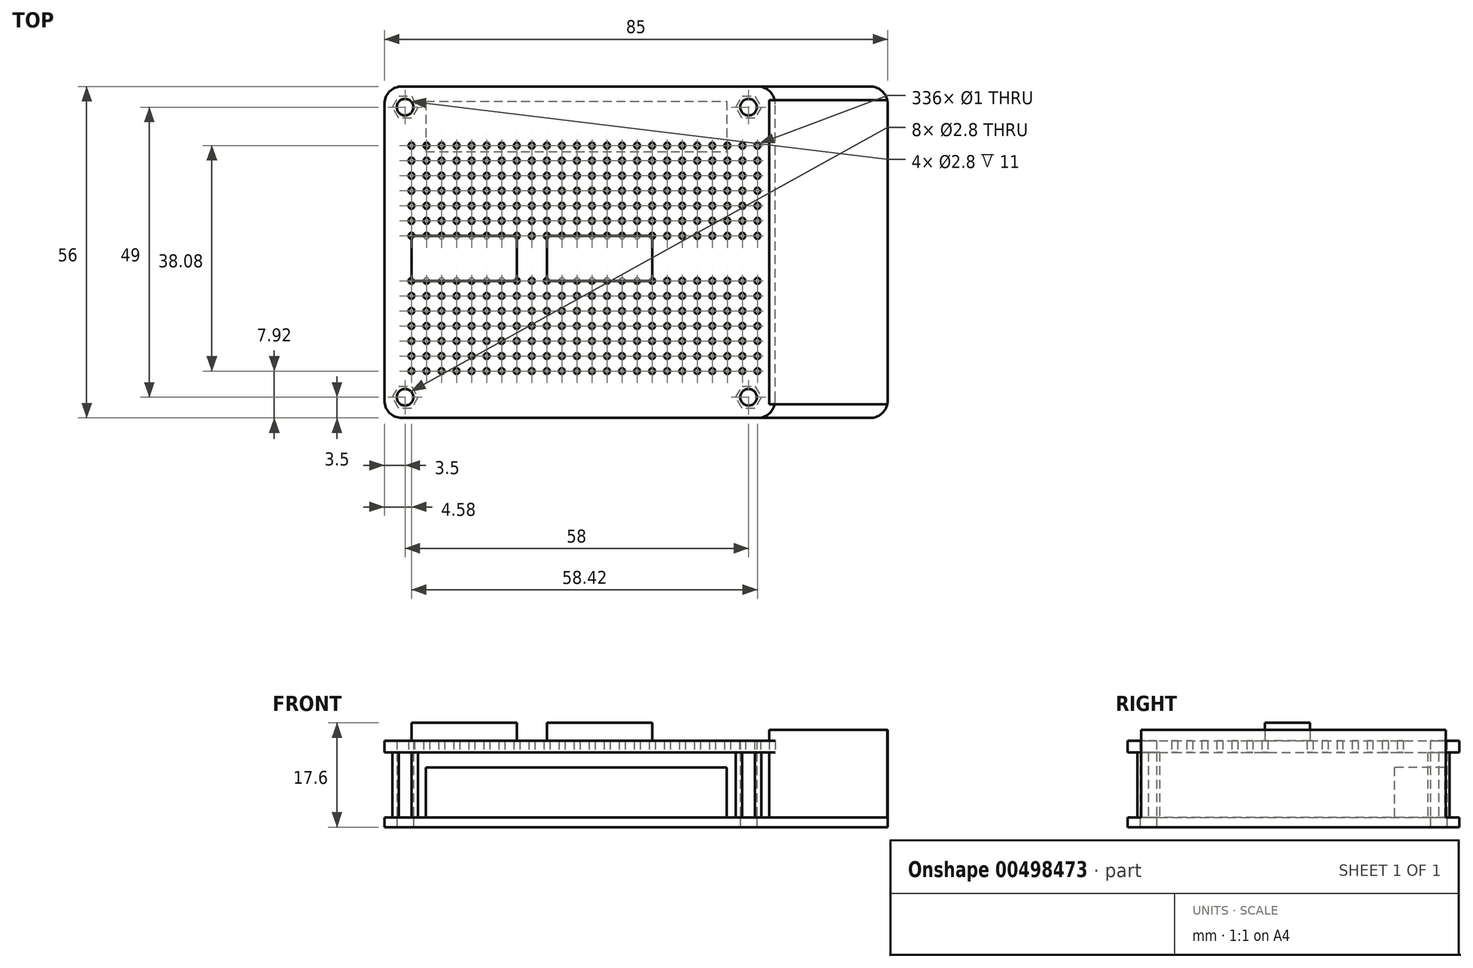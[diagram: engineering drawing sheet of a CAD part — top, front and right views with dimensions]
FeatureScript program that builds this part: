
annotation { "Feature Type Name" : "Feature", "Feature Type Description" : "" }
export const myFeature = defineFeature(function(context is Context, id is Id, definition is map)
    precondition{}
    {
        {
            var Q0;
            Q0=qCreatedBy(makeId("Top.planeOp"),FACE);
            var sketch = newSketch(context, id + "F0", { "sketchPlane" : qUnion([Q0])});
            skLineSegment(sketch, "E0.bottom", {"start": v(39.5, -28) * mm, "end": v(-39.5, -28) * mm});
            skLineSegment(sketch, "E0.top", {"start": v(39.5, 28) * mm, "end": v(-39.5, 28) * mm});
            skLineSegment(sketch, "E0.left", {"start": v(42.5, -25) * mm, "end": v(42.5, 25) * mm});
            skLineSegment(sketch, "E0.right", {"start": v(-42.5, -25) * mm, "end": v(-42.5, 25) * mm});
            skPoint(sketch, "E0.middle", {"position": v(0, 0) * mm});
            skLineSegment(sketch, "E1.bottom", {"start": v(-39, 24.5) * mm, "end": v(19, 24.5) * mm, "construction": true});
            skLineSegment(sketch, "E1.top", {"start": v(-39, -24.5) * mm, "end": v(19, -24.5) * mm, "construction": true});
            skLineSegment(sketch, "E1.left", {"start": v(-39, 24.5) * mm, "end": v(-39, -24.5) * mm, "construction": true});
            skLineSegment(sketch, "E1.right", {"start": v(19, 24.5) * mm, "end": v(19, -24.5) * mm, "construction": true});
            skCircle(sketch, "E2", {"center": v(-39, 24.5) * mm, "radius": 1.4 * mm});
            skCircle(sketch, "E3", {"center": v(19, 24.5) * mm, "radius": 1.4 * mm});
            skCircle(sketch, "E4", {"center": v(-39, -24.5) * mm, "radius": 1.4 * mm});
            skCircle(sketch, "E5", {"center": v(19, -24.5) * mm, "radius": 1.4 * mm});
            skPoint(sketch, "E6.visualSharp", {"position": v(-42.5, 28) * mm});
            skArc(sketch, "E6.filletArc", {"start": v(-39.5, 28) * mm, "mid": v(-41.62, 27.12) * mm, "end": v(-42.5, 25) * mm});
            skPoint(sketch, "E7.visualSharp", {"position": v(42.5, 28) * mm});
            skArc(sketch, "E7.filletArc", {"start": v(42.5, 25) * mm, "mid": v(41.62, 27.12) * mm, "end": v(39.5, 28) * mm});
            skPoint(sketch, "E8.visualSharp", {"position": v(42.5, -28) * mm});
            skArc(sketch, "E8.filletArc", {"start": v(39.5, -28) * mm, "mid": v(41.62, -27.12) * mm, "end": v(42.5, -25) * mm});
            skPoint(sketch, "E9.visualSharp", {"position": v(-42.5, -28) * mm});
            skArc(sketch, "E9.filletArc", {"start": v(-42.5, -25) * mm, "mid": v(-41.62, -27.12) * mm, "end": v(-39.5, -28) * mm});
            skSolve(sketch);
        }
        {
            var Q0;
            Q0 = qSketchRegion(id + "F0", true);
            extrude(context, id + "F1", {"entities" : qUnion([Q0]), "depth" : 1.6 * mm});
        }
        {
            var Q0;
            Q0=makeQuery(id+"F1.opExtrude","CAP_FACE",FACE,{"disambiguationData":[OSD([sQuery(id+"F0.wireOp",EDGE,"E0.bottom"),sQuery(id+"F0.wireOp",EDGE,"E0.top"),sQuery(id+"F0.wireOp",EDGE,"E0.left"),sQuery(id+"F0.wireOp",EDGE,"E0.right"),sQuery(id+"F0.wireOp",EDGE,"E2"),sQuery(id+"F0.wireOp",EDGE,"E3"),sQuery(id+"F0.wireOp",EDGE,"E4"),sQuery(id+"F0.wireOp",EDGE,"E5"),sQuery(id+"F0.wireOp",EDGE,"E6.filletArc"),sQuery(id+"F0.wireOp",EDGE,"E7.filletArc"),sQuery(id+"F0.wireOp",EDGE,"E8.filletArc"),sQuery(id+"F0.wireOp",EDGE,"E9.filletArc")])],"isStart":false});
            var sketch = newSketch(context, id + "F2", { "sketchPlane" : qUnion([Q0])});
            skLineSegment(sketch, "E10.bottom", {"start": v(22.5, 25.7) * mm, "end": v(42.5, 25.7) * mm});
            skLineSegment(sketch, "E10.top", {"start": v(22.5, -25.7) * mm, "end": v(42.5, -25.7) * mm});
            skLineSegment(sketch, "E10.left", {"start": v(22.5, 25.7) * mm, "end": v(22.5, -25.7) * mm});
            skLineSegment(sketch, "E10.right", {"start": v(42.5, 25.7) * mm, "end": v(42.5, -25.7) * mm});
            skSolve(sketch);
        }
        {
            var Q0;
            {var subQ0=sQuery(id+"F2.wireOp",EDGE,"E10.left");Q0=makeQuery(id+"F2.imprint","IMPRINT",FACE,{"disambiguationData":[TD([[makeQuery(id+"F2.imprint","IMPRINT",EDGE,{"derivedFrom":subQ0}),1.0]])]});}
            extrude(context, id + "F3", {"entities" : qUnion([Q0]), "operationType" : NewBodyOperationType.ADD, "depth" : 14.8 * mm});
        }
        {
            var Q0;
            Q0=makeQuery(id+"F1.opExtrude","CAP_FACE",FACE,{"disambiguationData":[OSD([sQuery(id+"F0.wireOp",EDGE,"E0.bottom"),sQuery(id+"F0.wireOp",EDGE,"E0.top"),sQuery(id+"F0.wireOp",EDGE,"E0.left"),sQuery(id+"F0.wireOp",EDGE,"E0.right"),sQuery(id+"F0.wireOp",EDGE,"E2"),sQuery(id+"F0.wireOp",EDGE,"E3"),sQuery(id+"F0.wireOp",EDGE,"E4"),sQuery(id+"F0.wireOp",EDGE,"E5"),sQuery(id+"F0.wireOp",EDGE,"E6.filletArc"),sQuery(id+"F0.wireOp",EDGE,"E7.filletArc"),sQuery(id+"F0.wireOp",EDGE,"E8.filletArc"),sQuery(id+"F0.wireOp",EDGE,"E9.filletArc")])],"isStart":false});
            var sketch = newSketch(context, id + "F4", { "sketchPlane" : qUnion([Q0])});
            skLineSegment(sketch, "E11.bottom", {"start": v(-35.5, 25.5) * mm, "end": v(15.3, 25.5) * mm});
            skLineSegment(sketch, "E11.top", {"start": v(-35.5, 17) * mm, "end": v(15.3, 17) * mm});
            skLineSegment(sketch, "E11.left", {"start": v(-35.5, 25.5) * mm, "end": v(-35.5, 17) * mm});
            skLineSegment(sketch, "E11.right", {"start": v(15.3, 25.5) * mm, "end": v(15.3, 17) * mm});
            skSolve(sketch);
        }
        {
            var Q0;
            Q0=makeQuery(id+"F4.imprint","IMPRINT",FACE,{"disambiguationData":[TD([[makeQuery(id+"F4.imprint","IMPRINT",EDGE,{"derivedFrom":sQuery(id+"F4.wireOp",EDGE,"E11.bottom")}),-1.0]])]});
            extrude(context, id + "F5", {"entities" : qUnion([Q0]), "operationType" : NewBodyOperationType.ADD, "depth" : 8.5 * mm});
        }
        {
            var Q0;
            Q0=makeQuery(id+"F1.opExtrude","CAP_FACE",FACE,{"disambiguationData":[OSD([sQuery(id+"F0.wireOp",EDGE,"E0.bottom"),sQuery(id+"F0.wireOp",EDGE,"E0.top"),sQuery(id+"F0.wireOp",EDGE,"E0.left"),sQuery(id+"F0.wireOp",EDGE,"E0.right"),sQuery(id+"F0.wireOp",EDGE,"E2"),sQuery(id+"F0.wireOp",EDGE,"E3"),sQuery(id+"F0.wireOp",EDGE,"E4"),sQuery(id+"F0.wireOp",EDGE,"E5"),sQuery(id+"F0.wireOp",EDGE,"E6.filletArc"),sQuery(id+"F0.wireOp",EDGE,"E7.filletArc"),sQuery(id+"F0.wireOp",EDGE,"E8.filletArc"),sQuery(id+"F0.wireOp",EDGE,"E9.filletArc")])],"isStart":false});
            var sketch = newSketch(context, id + "F6", { "sketchPlane" : qUnion([Q0])});
            skCircle(sketch, "E12", {"center": v(-39, 24.5) * mm, "radius": 1.4 * mm});
            skCircle(sketch, "E13", {"center": v(19, 24.5) * mm, "radius": 1.4 * mm});
            skCircle(sketch, "E14", {"center": v(-39, -24.5) * mm, "radius": 1.4 * mm});
            skCircle(sketch, "E15", {"center": v(19, -24.5) * mm, "radius": 1.4 * mm});
            skCircle(sketch, "E16.cCircle", {"center": v(-39, 24.5) * mm, "radius": 2.15 * mm, "construction": true});
            skLineSegment(sketch, "E16.0", {"start": v(-41.15, 24.5) * mm, "end": v(-40.08, 26.36) * mm});
            skLineSegment(sketch, "E16.1", {"start": v(-40.08, 26.36) * mm, "end": v(-37.93, 26.36) * mm});
            skLineSegment(sketch, "E16.2", {"start": v(-37.93, 26.36) * mm, "end": v(-36.85, 24.5) * mm});
            skLineSegment(sketch, "E16.3", {"start": v(-36.85, 24.5) * mm, "end": v(-37.93, 22.64) * mm});
            skLineSegment(sketch, "E16.4", {"start": v(-37.92, 22.64) * mm, "end": v(-40.08, 22.64) * mm});
            skLineSegment(sketch, "E16.5", {"start": v(-40.08, 22.64) * mm, "end": v(-41.15, 24.5) * mm});
            skCircle(sketch, "E17.cCircle", {"center": v(19, 24.5) * mm, "radius": 2.15 * mm, "construction": true});
            skLineSegment(sketch, "E17.0", {"start": v(16.85, 24.5) * mm, "end": v(17.92, 26.36) * mm});
            skLineSegment(sketch, "E17.1", {"start": v(17.92, 26.36) * mm, "end": v(20.07, 26.36) * mm});
            skLineSegment(sketch, "E17.2", {"start": v(20.07, 26.36) * mm, "end": v(21.15, 24.5) * mm});
            skLineSegment(sketch, "E17.3", {"start": v(21.15, 24.5) * mm, "end": v(20.07, 22.64) * mm});
            skLineSegment(sketch, "E17.4", {"start": v(20.07, 22.64) * mm, "end": v(17.92, 22.64) * mm});
            skLineSegment(sketch, "E17.5", {"start": v(17.92, 22.64) * mm, "end": v(16.85, 24.5) * mm});
            skCircle(sketch, "E18.cCircle", {"center": v(19, -24.5) * mm, "radius": 2.15 * mm, "construction": true});
            skLineSegment(sketch, "E18.0", {"start": v(16.85, -24.5) * mm, "end": v(17.93, -22.64) * mm});
            skLineSegment(sketch, "E18.1", {"start": v(17.93, -22.64) * mm, "end": v(20.08, -22.64) * mm});
            skLineSegment(sketch, "E18.2", {"start": v(20.08, -22.64) * mm, "end": v(21.15, -24.5) * mm});
            skLineSegment(sketch, "E18.3", {"start": v(21.15, -24.5) * mm, "end": v(20.08, -26.36) * mm});
            skLineSegment(sketch, "E18.4", {"start": v(20.08, -26.36) * mm, "end": v(17.93, -26.36) * mm});
            skLineSegment(sketch, "E18.5", {"start": v(17.93, -26.36) * mm, "end": v(16.85, -24.5) * mm});
            skCircle(sketch, "E19.cCircle", {"center": v(-39, -24.5) * mm, "radius": 2.15 * mm, "construction": true});
            skLineSegment(sketch, "E19.0", {"start": v(-36.85, -24.5) * mm, "end": v(-37.92, -26.36) * mm});
            skLineSegment(sketch, "E19.1", {"start": v(-37.92, -26.36) * mm, "end": v(-40.08, -26.36) * mm});
            skLineSegment(sketch, "E19.2", {"start": v(-40.07, -26.36) * mm, "end": v(-41.15, -24.5) * mm});
            skLineSegment(sketch, "E19.3", {"start": v(-41.15, -24.5) * mm, "end": v(-40.08, -22.64) * mm});
            skLineSegment(sketch, "E19.4", {"start": v(-40.07, -22.64) * mm, "end": v(-37.92, -22.64) * mm});
            skLineSegment(sketch, "E19.5", {"start": v(-37.92, -22.64) * mm, "end": v(-36.85, -24.5) * mm});
            skSolve(sketch);
        }
        {
            var Q0;
            Q0 = qSketchRegion(id + "F6", true);
            extrude(context, id + "F7", {"entities" : qUnion([Q0]), "depth" : 11 * mm});
        }
        {
            var Q0;
            Q0=makeQuery(id+"F7.opExtrude","CAP_FACE",FACE,{"disambiguationData":[OSD([sQuery(id+"F6.wireOp",EDGE,"E14"),sQuery(id+"F6.wireOp",EDGE,"E19.0"),sQuery(id+"F6.wireOp",EDGE,"E19.1"),sQuery(id+"F6.wireOp",EDGE,"E19.2"),sQuery(id+"F6.wireOp",EDGE,"E19.3"),sQuery(id+"F6.wireOp",EDGE,"E19.4"),sQuery(id+"F6.wireOp",EDGE,"E19.5")])],"isStart":false});
            var sketch = newSketch(context, id + "F8", { "sketchPlane" : qUnion([Q0])});
            skLineSegment(sketch, "E20.bottom", {"start": v(20.5, -28) * mm, "end": v(-39.5, -28) * mm});
            skLineSegment(sketch, "E20.top", {"start": v(20.5, 28) * mm, "end": v(-39.5, 28) * mm});
            skLineSegment(sketch, "E20.left", {"start": v(23.5, -25) * mm, "end": v(23.5, 25) * mm});
            skLineSegment(sketch, "E20.right", {"start": v(-42.5, -25) * mm, "end": v(-42.5, 25) * mm});
            skPoint(sketch, "E20.middle", {"position": v(-9.5, 0) * mm});
            skLineSegment(sketch, "E21.bottom", {"start": v(-39, 24.5) * mm, "end": v(19, 24.5) * mm, "construction": true});
            skLineSegment(sketch, "E21.top", {"start": v(-39, -24.5) * mm, "end": v(19, -24.5) * mm, "construction": true});
            skLineSegment(sketch, "E21.left", {"start": v(-39, 24.5) * mm, "end": v(-39, -24.5) * mm, "construction": true});
            skLineSegment(sketch, "E21.right", {"start": v(19, 24.5) * mm, "end": v(19, -24.5) * mm, "construction": true});
            skCircle(sketch, "E22", {"center": v(-39, 24.5) * mm, "radius": 1.4 * mm});
            skCircle(sketch, "E23", {"center": v(19, 24.5) * mm, "radius": 1.4 * mm});
            skCircle(sketch, "E24", {"center": v(-39, -24.5) * mm, "radius": 1.4 * mm});
            skCircle(sketch, "E25", {"center": v(19, -24.5) * mm, "radius": 1.4 * mm});
            skPoint(sketch, "E26.visualSharp", {"position": v(-42.5, 28) * mm});
            skArc(sketch, "E26.filletArc", {"start": v(-39.5, 28) * mm, "mid": v(-41.62, 27.12) * mm, "end": v(-42.5, 25) * mm});
            skPoint(sketch, "E27.visualSharp", {"position": v(23.5, 28) * mm});
            skArc(sketch, "E27.filletArc", {"start": v(23.5, 25) * mm, "mid": v(22.62, 27.12) * mm, "end": v(20.5, 28) * mm});
            skPoint(sketch, "E28.visualSharp", {"position": v(23.5, -28) * mm});
            skArc(sketch, "E28.filletArc", {"start": v(20.5, -28) * mm, "mid": v(22.62, -27.12) * mm, "end": v(23.5, -25) * mm});
            skPoint(sketch, "E29.visualSharp", {"position": v(-42.5, -28) * mm});
            skArc(sketch, "E29.filletArc", {"start": v(-42.5, -25) * mm, "mid": v(-41.62, -27.12) * mm, "end": v(-39.5, -28) * mm});
            skLineSegment(sketch, "E30.bottom", {"start": v(20.5, 18) * mm, "end": v(-37.92, 18) * mm, "construction": true});
            skLineSegment(sketch, "E30.top", {"start": v(20.5, 2.76) * mm, "end": v(-37.92, 2.76) * mm, "construction": true});
            skLineSegment(sketch, "E30.left", {"start": v(20.5, 18) * mm, "end": v(20.5, 2.76) * mm, "construction": true});
            skLineSegment(sketch, "E30.right", {"start": v(-37.92, 18) * mm, "end": v(-37.92, 2.76) * mm, "construction": true});
            skCircle(sketch, "E31", {"center": v(20.5, 18) * mm, "radius": 0.5 * mm});
            skCircle(sketch, "E32.0.1.0", {"center": v(20.5, 15.46) * mm, "radius": 0.5 * mm});
            skCircle(sketch, "E32.0.2.0", {"center": v(20.5, 12.92) * mm, "radius": 0.5 * mm});
            skCircle(sketch, "E32.0.3.0", {"center": v(20.5, 10.38) * mm, "radius": 0.5 * mm});
            skCircle(sketch, "E32.0.4.0", {"center": v(20.5, 7.84) * mm, "radius": 0.5 * mm});
            skCircle(sketch, "E32.0.5.0", {"center": v(20.5, 5.3) * mm, "radius": 0.5 * mm});
            skCircle(sketch, "E32.0.6.0", {"center": v(20.5, 2.76) * mm, "radius": 0.5 * mm});
            skCircle(sketch, "E32.1.0.0", {"center": v(17.96, 18) * mm, "radius": 0.5 * mm});
            skCircle(sketch, "E32.1.1.0", {"center": v(17.96, 15.46) * mm, "radius": 0.5 * mm});
            skCircle(sketch, "E32.1.2.0", {"center": v(17.96, 12.92) * mm, "radius": 0.5 * mm});
            skCircle(sketch, "E32.1.3.0", {"center": v(17.96, 10.38) * mm, "radius": 0.5 * mm});
            skCircle(sketch, "E32.1.4.0", {"center": v(17.96, 7.84) * mm, "radius": 0.5 * mm});
            skCircle(sketch, "E32.1.5.0", {"center": v(17.96, 5.3) * mm, "radius": 0.5 * mm});
            skCircle(sketch, "E32.1.6.0", {"center": v(17.96, 2.76) * mm, "radius": 0.5 * mm});
            skCircle(sketch, "E32.2.0.0", {"center": v(15.42, 18) * mm, "radius": 0.5 * mm});
            skCircle(sketch, "E32.2.1.0", {"center": v(15.42, 15.46) * mm, "radius": 0.5 * mm});
            skCircle(sketch, "E32.2.2.0", {"center": v(15.42, 12.92) * mm, "radius": 0.5 * mm});
            skCircle(sketch, "E32.2.3.0", {"center": v(15.42, 10.38) * mm, "radius": 0.5 * mm});
            skCircle(sketch, "E32.2.4.0", {"center": v(15.42, 7.84) * mm, "radius": 0.5 * mm});
            skCircle(sketch, "E32.2.5.0", {"center": v(15.42, 5.3) * mm, "radius": 0.5 * mm});
            skCircle(sketch, "E32.2.6.0", {"center": v(15.42, 2.76) * mm, "radius": 0.5 * mm});
            skCircle(sketch, "E32.3.0.0", {"center": v(12.88, 18) * mm, "radius": 0.5 * mm});
            skCircle(sketch, "E32.3.1.0", {"center": v(12.88, 15.46) * mm, "radius": 0.5 * mm});
            skCircle(sketch, "E32.3.2.0", {"center": v(12.88, 12.92) * mm, "radius": 0.5 * mm});
            skCircle(sketch, "E32.3.3.0", {"center": v(12.88, 10.38) * mm, "radius": 0.5 * mm});
            skCircle(sketch, "E32.3.4.0", {"center": v(12.88, 7.84) * mm, "radius": 0.5 * mm});
            skCircle(sketch, "E32.3.5.0", {"center": v(12.88, 5.3) * mm, "radius": 0.5 * mm});
            skCircle(sketch, "E32.3.6.0", {"center": v(12.88, 2.76) * mm, "radius": 0.5 * mm});
            skCircle(sketch, "E32.4.0.0", {"center": v(10.34, 18) * mm, "radius": 0.5 * mm});
            skCircle(sketch, "E32.4.1.0", {"center": v(10.34, 15.46) * mm, "radius": 0.5 * mm});
            skCircle(sketch, "E32.4.2.0", {"center": v(10.34, 12.92) * mm, "radius": 0.5 * mm});
            skCircle(sketch, "E32.4.3.0", {"center": v(10.34, 10.38) * mm, "radius": 0.5 * mm});
            skCircle(sketch, "E32.4.4.0", {"center": v(10.34, 7.84) * mm, "radius": 0.5 * mm});
            skCircle(sketch, "E32.4.5.0", {"center": v(10.34, 5.3) * mm, "radius": 0.5 * mm});
            skCircle(sketch, "E32.4.6.0", {"center": v(10.34, 2.76) * mm, "radius": 0.5 * mm});
            skCircle(sketch, "E32.5.0.0", {"center": v(7.8, 18) * mm, "radius": 0.5 * mm});
            skCircle(sketch, "E32.5.1.0", {"center": v(7.8, 15.46) * mm, "radius": 0.5 * mm});
            skCircle(sketch, "E32.5.2.0", {"center": v(7.8, 12.92) * mm, "radius": 0.5 * mm});
            skCircle(sketch, "E32.5.3.0", {"center": v(7.8, 10.38) * mm, "radius": 0.5 * mm});
            skCircle(sketch, "E32.5.4.0", {"center": v(7.8, 7.84) * mm, "radius": 0.5 * mm});
            skCircle(sketch, "E32.5.5.0", {"center": v(7.8, 5.3) * mm, "radius": 0.5 * mm});
            skCircle(sketch, "E32.5.6.0", {"center": v(7.8, 2.76) * mm, "radius": 0.5 * mm});
            skCircle(sketch, "E32.6.0.0", {"center": v(5.26, 18) * mm, "radius": 0.5 * mm});
            skCircle(sketch, "E32.6.1.0", {"center": v(5.26, 15.46) * mm, "radius": 0.5 * mm});
            skCircle(sketch, "E32.6.2.0", {"center": v(5.26, 12.92) * mm, "radius": 0.5 * mm});
            skCircle(sketch, "E32.6.3.0", {"center": v(5.26, 10.38) * mm, "radius": 0.5 * mm});
            skCircle(sketch, "E32.6.4.0", {"center": v(5.26, 7.84) * mm, "radius": 0.5 * mm});
            skCircle(sketch, "E32.6.5.0", {"center": v(5.26, 5.3) * mm, "radius": 0.5 * mm});
            skCircle(sketch, "E32.6.6.0", {"center": v(5.26, 2.76) * mm, "radius": 0.5 * mm});
            skCircle(sketch, "E32.7.0.0", {"center": v(2.72, 18) * mm, "radius": 0.5 * mm});
            skCircle(sketch, "E32.7.1.0", {"center": v(2.72, 15.46) * mm, "radius": 0.5 * mm});
            skCircle(sketch, "E32.7.2.0", {"center": v(2.72, 12.92) * mm, "radius": 0.5 * mm});
            skCircle(sketch, "E32.7.3.0", {"center": v(2.72, 10.38) * mm, "radius": 0.5 * mm});
            skCircle(sketch, "E32.7.4.0", {"center": v(2.72, 7.84) * mm, "radius": 0.5 * mm});
            skCircle(sketch, "E32.7.5.0", {"center": v(2.72, 5.3) * mm, "radius": 0.5 * mm});
            skCircle(sketch, "E32.7.6.0", {"center": v(2.72, 2.76) * mm, "radius": 0.5 * mm});
            skCircle(sketch, "E32.8.0.0", {"center": v(0.18, 18) * mm, "radius": 0.5 * mm});
            skCircle(sketch, "E32.8.1.0", {"center": v(0.18, 15.46) * mm, "radius": 0.5 * mm});
            skCircle(sketch, "E32.8.2.0", {"center": v(0.18, 12.92) * mm, "radius": 0.5 * mm});
            skCircle(sketch, "E32.8.3.0", {"center": v(0.18, 10.38) * mm, "radius": 0.5 * mm});
            skCircle(sketch, "E32.8.4.0", {"center": v(0.18, 7.84) * mm, "radius": 0.5 * mm});
            skCircle(sketch, "E32.8.5.0", {"center": v(0.18, 5.3) * mm, "radius": 0.5 * mm});
            skCircle(sketch, "E32.8.6.0", {"center": v(0.18, 2.76) * mm, "radius": 0.5 * mm});
            skCircle(sketch, "E32.9.0.0", {"center": v(-2.36, 18) * mm, "radius": 0.5 * mm});
            skCircle(sketch, "E32.9.1.0", {"center": v(-2.36, 15.46) * mm, "radius": 0.5 * mm});
            skCircle(sketch, "E32.9.2.0", {"center": v(-2.36, 12.92) * mm, "radius": 0.5 * mm});
            skCircle(sketch, "E32.9.3.0", {"center": v(-2.36, 10.38) * mm, "radius": 0.5 * mm});
            skCircle(sketch, "E32.9.4.0", {"center": v(-2.36, 7.84) * mm, "radius": 0.5 * mm});
            skCircle(sketch, "E32.9.5.0", {"center": v(-2.36, 5.3) * mm, "radius": 0.5 * mm});
            skCircle(sketch, "E32.9.6.0", {"center": v(-2.36, 2.76) * mm, "radius": 0.5 * mm});
            skCircle(sketch, "E32.10.0.0", {"center": v(-4.9, 18) * mm, "radius": 0.5 * mm});
            skCircle(sketch, "E32.10.1.0", {"center": v(-4.9, 15.46) * mm, "radius": 0.5 * mm});
            skCircle(sketch, "E32.10.2.0", {"center": v(-4.9, 12.92) * mm, "radius": 0.5 * mm});
            skCircle(sketch, "E32.10.3.0", {"center": v(-4.9, 10.38) * mm, "radius": 0.5 * mm});
            skCircle(sketch, "E32.10.4.0", {"center": v(-4.9, 7.84) * mm, "radius": 0.5 * mm});
            skCircle(sketch, "E32.10.5.0", {"center": v(-4.9, 5.3) * mm, "radius": 0.5 * mm});
            skCircle(sketch, "E32.10.6.0", {"center": v(-4.9, 2.76) * mm, "radius": 0.5 * mm});
            skCircle(sketch, "E32.11.0.0", {"center": v(-7.44, 18) * mm, "radius": 0.5 * mm});
            skCircle(sketch, "E32.11.1.0", {"center": v(-7.44, 15.46) * mm, "radius": 0.5 * mm});
            skCircle(sketch, "E32.11.2.0", {"center": v(-7.44, 12.92) * mm, "radius": 0.5 * mm});
            skCircle(sketch, "E32.11.3.0", {"center": v(-7.44, 10.38) * mm, "radius": 0.5 * mm});
            skCircle(sketch, "E32.11.4.0", {"center": v(-7.44, 7.84) * mm, "radius": 0.5 * mm});
            skCircle(sketch, "E32.11.5.0", {"center": v(-7.44, 5.3) * mm, "radius": 0.5 * mm});
            skCircle(sketch, "E32.11.6.0", {"center": v(-7.44, 2.76) * mm, "radius": 0.5 * mm});
            skCircle(sketch, "E32.12.0.0", {"center": v(-9.98, 18) * mm, "radius": 0.5 * mm});
            skCircle(sketch, "E32.12.1.0", {"center": v(-9.98, 15.46) * mm, "radius": 0.5 * mm});
            skCircle(sketch, "E32.12.2.0", {"center": v(-9.98, 12.92) * mm, "radius": 0.5 * mm});
            skCircle(sketch, "E32.12.3.0", {"center": v(-9.98, 10.38) * mm, "radius": 0.5 * mm});
            skCircle(sketch, "E32.12.4.0", {"center": v(-9.98, 7.84) * mm, "radius": 0.5 * mm});
            skCircle(sketch, "E32.12.5.0", {"center": v(-9.98, 5.3) * mm, "radius": 0.5 * mm});
            skCircle(sketch, "E32.12.6.0", {"center": v(-9.98, 2.76) * mm, "radius": 0.5 * mm});
            skCircle(sketch, "E32.13.0.0", {"center": v(-12.52, 18) * mm, "radius": 0.5 * mm});
            skCircle(sketch, "E32.13.1.0", {"center": v(-12.52, 15.46) * mm, "radius": 0.5 * mm});
            skCircle(sketch, "E32.13.2.0", {"center": v(-12.52, 12.92) * mm, "radius": 0.5 * mm});
            skCircle(sketch, "E32.13.3.0", {"center": v(-12.52, 10.38) * mm, "radius": 0.5 * mm});
            skCircle(sketch, "E32.13.4.0", {"center": v(-12.52, 7.84) * mm, "radius": 0.5 * mm});
            skCircle(sketch, "E32.13.5.0", {"center": v(-12.52, 5.3) * mm, "radius": 0.5 * mm});
            skCircle(sketch, "E32.13.6.0", {"center": v(-12.52, 2.76) * mm, "radius": 0.5 * mm});
            skCircle(sketch, "E32.14.0.0", {"center": v(-15.06, 18) * mm, "radius": 0.5 * mm});
            skCircle(sketch, "E32.14.1.0", {"center": v(-15.06, 15.46) * mm, "radius": 0.5 * mm});
            skCircle(sketch, "E32.14.2.0", {"center": v(-15.06, 12.92) * mm, "radius": 0.5 * mm});
            skCircle(sketch, "E32.14.3.0", {"center": v(-15.06, 10.38) * mm, "radius": 0.5 * mm});
            skCircle(sketch, "E32.14.4.0", {"center": v(-15.06, 7.84) * mm, "radius": 0.5 * mm});
            skCircle(sketch, "E32.14.5.0", {"center": v(-15.06, 5.3) * mm, "radius": 0.5 * mm});
            skCircle(sketch, "E32.14.6.0", {"center": v(-15.06, 2.76) * mm, "radius": 0.5 * mm});
            skCircle(sketch, "E32.15.0.0", {"center": v(-17.6, 18) * mm, "radius": 0.5 * mm});
            skCircle(sketch, "E32.15.1.0", {"center": v(-17.6, 15.46) * mm, "radius": 0.5 * mm});
            skCircle(sketch, "E32.15.2.0", {"center": v(-17.6, 12.92) * mm, "radius": 0.5 * mm});
            skCircle(sketch, "E32.15.3.0", {"center": v(-17.6, 10.38) * mm, "radius": 0.5 * mm});
            skCircle(sketch, "E32.15.4.0", {"center": v(-17.6, 7.84) * mm, "radius": 0.5 * mm});
            skCircle(sketch, "E32.15.5.0", {"center": v(-17.6, 5.3) * mm, "radius": 0.5 * mm});
            skCircle(sketch, "E32.15.6.0", {"center": v(-17.6, 2.76) * mm, "radius": 0.5 * mm});
            skCircle(sketch, "E32.16.0.0", {"center": v(-20.14, 18) * mm, "radius": 0.5 * mm});
            skCircle(sketch, "E32.16.1.0", {"center": v(-20.14, 15.46) * mm, "radius": 0.5 * mm});
            skCircle(sketch, "E32.16.2.0", {"center": v(-20.14, 12.92) * mm, "radius": 0.5 * mm});
            skCircle(sketch, "E32.16.3.0", {"center": v(-20.14, 10.38) * mm, "radius": 0.5 * mm});
            skCircle(sketch, "E32.16.4.0", {"center": v(-20.14, 7.84) * mm, "radius": 0.5 * mm});
            skCircle(sketch, "E32.16.5.0", {"center": v(-20.14, 5.3) * mm, "radius": 0.5 * mm});
            skCircle(sketch, "E32.16.6.0", {"center": v(-20.14, 2.76) * mm, "radius": 0.5 * mm});
            skCircle(sketch, "E32.17.0.0", {"center": v(-22.68, 18) * mm, "radius": 0.5 * mm});
            skCircle(sketch, "E32.17.1.0", {"center": v(-22.68, 15.46) * mm, "radius": 0.5 * mm});
            skCircle(sketch, "E32.17.2.0", {"center": v(-22.68, 12.92) * mm, "radius": 0.5 * mm});
            skCircle(sketch, "E32.17.3.0", {"center": v(-22.68, 10.38) * mm, "radius": 0.5 * mm});
            skCircle(sketch, "E32.17.4.0", {"center": v(-22.68, 7.84) * mm, "radius": 0.5 * mm});
            skCircle(sketch, "E32.17.5.0", {"center": v(-22.68, 5.3) * mm, "radius": 0.5 * mm});
            skCircle(sketch, "E32.17.6.0", {"center": v(-22.68, 2.76) * mm, "radius": 0.5 * mm});
            skCircle(sketch, "E32.18.0.0", {"center": v(-25.22, 18) * mm, "radius": 0.5 * mm});
            skCircle(sketch, "E32.18.1.0", {"center": v(-25.22, 15.46) * mm, "radius": 0.5 * mm});
            skCircle(sketch, "E32.18.2.0", {"center": v(-25.22, 12.92) * mm, "radius": 0.5 * mm});
            skCircle(sketch, "E32.18.3.0", {"center": v(-25.22, 10.38) * mm, "radius": 0.5 * mm});
            skCircle(sketch, "E32.18.4.0", {"center": v(-25.22, 7.84) * mm, "radius": 0.5 * mm});
            skCircle(sketch, "E32.18.5.0", {"center": v(-25.22, 5.3) * mm, "radius": 0.5 * mm});
            skCircle(sketch, "E32.18.6.0", {"center": v(-25.22, 2.76) * mm, "radius": 0.5 * mm});
            skCircle(sketch, "E32.19.0.0", {"center": v(-27.76, 18) * mm, "radius": 0.5 * mm});
            skCircle(sketch, "E32.19.1.0", {"center": v(-27.76, 15.46) * mm, "radius": 0.5 * mm});
            skCircle(sketch, "E32.19.2.0", {"center": v(-27.76, 12.92) * mm, "radius": 0.5 * mm});
            skCircle(sketch, "E32.19.3.0", {"center": v(-27.76, 10.38) * mm, "radius": 0.5 * mm});
            skCircle(sketch, "E32.19.4.0", {"center": v(-27.76, 7.84) * mm, "radius": 0.5 * mm});
            skCircle(sketch, "E32.19.5.0", {"center": v(-27.76, 5.3) * mm, "radius": 0.5 * mm});
            skCircle(sketch, "E32.19.6.0", {"center": v(-27.76, 2.76) * mm, "radius": 0.5 * mm});
            skCircle(sketch, "E32.20.0.0", {"center": v(-30.3, 18) * mm, "radius": 0.5 * mm});
            skCircle(sketch, "E32.20.1.0", {"center": v(-30.3, 15.46) * mm, "radius": 0.5 * mm});
            skCircle(sketch, "E32.20.2.0", {"center": v(-30.3, 12.92) * mm, "radius": 0.5 * mm});
            skCircle(sketch, "E32.20.3.0", {"center": v(-30.3, 10.38) * mm, "radius": 0.5 * mm});
            skCircle(sketch, "E32.20.4.0", {"center": v(-30.3, 7.84) * mm, "radius": 0.5 * mm});
            skCircle(sketch, "E32.20.5.0", {"center": v(-30.3, 5.3) * mm, "radius": 0.5 * mm});
            skCircle(sketch, "E32.20.6.0", {"center": v(-30.3, 2.76) * mm, "radius": 0.5 * mm});
            skCircle(sketch, "E32.21.0.0", {"center": v(-32.84, 18) * mm, "radius": 0.5 * mm});
            skCircle(sketch, "E32.21.1.0", {"center": v(-32.84, 15.46) * mm, "radius": 0.5 * mm});
            skCircle(sketch, "E32.21.2.0", {"center": v(-32.84, 12.92) * mm, "radius": 0.5 * mm});
            skCircle(sketch, "E32.21.3.0", {"center": v(-32.84, 10.38) * mm, "radius": 0.5 * mm});
            skCircle(sketch, "E32.21.4.0", {"center": v(-32.84, 7.84) * mm, "radius": 0.5 * mm});
            skCircle(sketch, "E32.21.5.0", {"center": v(-32.84, 5.3) * mm, "radius": 0.5 * mm});
            skCircle(sketch, "E32.21.6.0", {"center": v(-32.84, 2.76) * mm, "radius": 0.5 * mm});
            skCircle(sketch, "E32.22.0.0", {"center": v(-35.38, 18) * mm, "radius": 0.5 * mm});
            skCircle(sketch, "E32.22.1.0", {"center": v(-35.38, 15.46) * mm, "radius": 0.5 * mm});
            skCircle(sketch, "E32.22.2.0", {"center": v(-35.38, 12.92) * mm, "radius": 0.5 * mm});
            skCircle(sketch, "E32.22.3.0", {"center": v(-35.38, 10.38) * mm, "radius": 0.5 * mm});
            skCircle(sketch, "E32.22.4.0", {"center": v(-35.38, 7.84) * mm, "radius": 0.5 * mm});
            skCircle(sketch, "E32.22.5.0", {"center": v(-35.38, 5.3) * mm, "radius": 0.5 * mm});
            skCircle(sketch, "E32.22.6.0", {"center": v(-35.38, 2.76) * mm, "radius": 0.5 * mm});
            skCircle(sketch, "E32.23.0.0", {"center": v(-37.92, 18) * mm, "radius": 0.5 * mm});
            skCircle(sketch, "E32.23.1.0", {"center": v(-37.92, 15.46) * mm, "radius": 0.5 * mm});
            skCircle(sketch, "E32.23.2.0", {"center": v(-37.92, 12.92) * mm, "radius": 0.5 * mm});
            skCircle(sketch, "E32.23.3.0", {"center": v(-37.92, 10.38) * mm, "radius": 0.5 * mm});
            skCircle(sketch, "E32.23.4.0", {"center": v(-37.92, 7.84) * mm, "radius": 0.5 * mm});
            skCircle(sketch, "E32.23.5.0", {"center": v(-37.92, 5.3) * mm, "radius": 0.5 * mm});
            skCircle(sketch, "E32.23.6.0", {"center": v(-37.92, 2.76) * mm, "radius": 0.5 * mm});
            skLineSegment(sketch, "E32.direction1", {"start": v(20.5, 18) * mm, "end": v(17.96, 18) * mm, "construction": true});
            skLineSegment(sketch, "E32.direction2", {"start": v(20.5, 18) * mm, "end": v(20.5, 15.46) * mm, "construction": true});
            skLineSegment(sketch, "E33", {"start": v(-39, -1.04) * mm, "end": v(19, -1.04) * mm, "construction": true});
            skCircle(sketch, "E34.MirrorC", {"center": v(20.5, -20.08) * mm, "radius": 0.5 * mm});
            skCircle(sketch, "E35.MirrorC", {"center": v(-37.92, -20.08) * mm, "radius": 0.5 * mm});
            skCircle(sketch, "E36.MirrorC", {"center": v(-37.92, -4.84) * mm, "radius": 0.5 * mm});
            skCircle(sketch, "E37.MirrorC", {"center": v(20.5, -4.84) * mm, "radius": 0.5 * mm});
            skCircle(sketch, "E38.MirrorC", {"center": v(20.5, -17.54) * mm, "radius": 0.5 * mm});
            skCircle(sketch, "E39.MirrorC", {"center": v(17.96, -20.08) * mm, "radius": 0.5 * mm});
            skCircle(sketch, "E40.MirrorC", {"center": v(-4.9, -9.92) * mm, "radius": 0.5 * mm});
            skCircle(sketch, "E41.MirrorC", {"center": v(0.18, -15) * mm, "radius": 0.5 * mm});
            skCircle(sketch, "E42.MirrorC", {"center": v(-37.92, -15) * mm, "radius": 0.5 * mm});
            skCircle(sketch, "E43.MirrorC", {"center": v(-32.84, -20.08) * mm, "radius": 0.5 * mm});
            skCircle(sketch, "E44.MirrorC", {"center": v(-20.14, -12.46) * mm, "radius": 0.5 * mm});
            skCircle(sketch, "E45.MirrorC", {"center": v(-15.06, -17.54) * mm, "radius": 0.5 * mm});
            skCircle(sketch, "E46.MirrorC", {"center": v(-7.44, -4.84) * mm, "radius": 0.5 * mm});
            skCircle(sketch, "E47.MirrorC", {"center": v(10.34, -9.92) * mm, "radius": 0.5 * mm});
            skCircle(sketch, "E48.MirrorC", {"center": v(10.34, -12.46) * mm, "radius": 0.5 * mm});
            skCircle(sketch, "E49.MirrorC", {"center": v(-17.6, -4.84) * mm, "radius": 0.5 * mm});
            skCircle(sketch, "E50.MirrorC", {"center": v(-17.6, -7.38) * mm, "radius": 0.5 * mm});
            skCircle(sketch, "E51.MirrorC", {"center": v(5.26, -9.92) * mm, "radius": 0.5 * mm});
            skCircle(sketch, "E52.MirrorC", {"center": v(-30.3, -15) * mm, "radius": 0.5 * mm});
            skCircle(sketch, "E53.MirrorC", {"center": v(-25.22, -20.08) * mm, "radius": 0.5 * mm});
            skCircle(sketch, "E54.MirrorC", {"center": v(-35.38, -9.92) * mm, "radius": 0.5 * mm});
            skCircle(sketch, "E55.MirrorC", {"center": v(-20.14, -15) * mm, "radius": 0.5 * mm});
            skCircle(sketch, "E56.MirrorC", {"center": v(-2.36, -12.46) * mm, "radius": 0.5 * mm});
            skCircle(sketch, "E57.MirrorC", {"center": v(2.72, -17.54) * mm, "radius": 0.5 * mm});
            skCircle(sketch, "E58.MirrorC", {"center": v(-30.3, -4.84) * mm, "radius": 0.5 * mm});
            skCircle(sketch, "E59.MirrorC", {"center": v(-25.22, -9.92) * mm, "radius": 0.5 * mm});
            skCircle(sketch, "E60.MirrorC", {"center": v(20.5, -15) * mm, "radius": 0.5 * mm});
            skCircle(sketch, "E61.MirrorC", {"center": v(-15.06, -20.08) * mm, "radius": 0.5 * mm});
            skCircle(sketch, "E62.MirrorC", {"center": v(10.34, -4.84) * mm, "radius": 0.5 * mm});
            skCircle(sketch, "E63.MirrorC", {"center": v(-25.22, -12.46) * mm, "radius": 0.5 * mm});
            skCircle(sketch, "E64.MirrorC", {"center": v(2.72, -20.08) * mm, "radius": 0.5 * mm});
            skCircle(sketch, "E65.MirrorC", {"center": v(10.34, -7.38) * mm, "radius": 0.5 * mm});
            skCircle(sketch, "E66.MirrorC", {"center": v(-2.36, -20.08) * mm, "radius": 0.5 * mm});
            skCircle(sketch, "E67.MirrorC", {"center": v(-35.38, -7.38) * mm, "radius": 0.5 * mm});
            skCircle(sketch, "E68.MirrorC", {"center": v(2.72, -12.46) * mm, "radius": 0.5 * mm});
            skCircle(sketch, "E69.MirrorC", {"center": v(-20.14, -20.08) * mm, "radius": 0.5 * mm});
            skCircle(sketch, "E70.MirrorC", {"center": v(-35.38, -4.84) * mm, "radius": 0.5 * mm});
            skCircle(sketch, "E71.MirrorC", {"center": v(-25.22, -17.54) * mm, "radius": 0.5 * mm});
            skCircle(sketch, "E72.MirrorC", {"center": v(10.34, -15) * mm, "radius": 0.5 * mm});
            skCircle(sketch, "E73.MirrorC", {"center": v(5.26, -12.46) * mm, "radius": 0.5 * mm});
            skCircle(sketch, "E74.MirrorC", {"center": v(-30.3, -17.54) * mm, "radius": 0.5 * mm});
            skCircle(sketch, "E75.MirrorC", {"center": v(-17.6, -9.92) * mm, "radius": 0.5 * mm});
            skCircle(sketch, "E76.MirrorC", {"center": v(0.18, -4.84) * mm, "radius": 0.5 * mm});
            skCircle(sketch, "E77.MirrorC", {"center": v(15.42, -20.08) * mm, "radius": 0.5 * mm});
            skCircle(sketch, "E78.MirrorC", {"center": v(10.34, -17.54) * mm, "radius": 0.5 * mm});
            skCircle(sketch, "E79.MirrorC", {"center": v(17.96, -4.84) * mm, "radius": 0.5 * mm});
            skCircle(sketch, "E80.MirrorC", {"center": v(-12.52, -4.84) * mm, "radius": 0.5 * mm});
            skCircle(sketch, "E81.MirrorC", {"center": v(-2.36, -15) * mm, "radius": 0.5 * mm});
            skCircle(sketch, "E82.MirrorC", {"center": v(-17.6, -12.46) * mm, "radius": 0.5 * mm});
            skCircle(sketch, "E83.MirrorC", {"center": v(-12.52, -17.54) * mm, "radius": 0.5 * mm});
            skCircle(sketch, "E84.MirrorC", {"center": v(10.34, -20.08) * mm, "radius": 0.5 * mm});
            skCircle(sketch, "E85.MirrorC", {"center": v(-22.68, -9.92) * mm, "radius": 0.5 * mm});
            skCircle(sketch, "E86.MirrorC", {"center": v(0.18, -12.46) * mm, "radius": 0.5 * mm});
            skCircle(sketch, "E87.MirrorC", {"center": v(12.88, -4.84) * mm, "radius": 0.5 * mm});
            skCircle(sketch, "E88.MirrorC", {"center": v(17.96, -9.92) * mm, "radius": 0.5 * mm});
            skCircle(sketch, "E89.MirrorC", {"center": v(-12.52, -20.08) * mm, "radius": 0.5 * mm});
            skCircle(sketch, "E90.MirrorC", {"center": v(-4.9, -7.38) * mm, "radius": 0.5 * mm});
            skCircle(sketch, "E91.MirrorC", {"center": v(-22.68, -12.46) * mm, "radius": 0.5 * mm});
            skCircle(sketch, "E92.MirrorC", {"center": v(-17.6, -17.54) * mm, "radius": 0.5 * mm});
            skCircle(sketch, "E93.MirrorC", {"center": v(-27.76, -7.38) * mm, "radius": 0.5 * mm});
            skCircle(sketch, "E94.MirrorC", {"center": v(17.96, -12.46) * mm, "radius": 0.5 * mm});
            skCircle(sketch, "E95.MirrorC", {"center": v(-32.84, -7.38) * mm, "radius": 0.5 * mm});
            skCircle(sketch, "E96.MirrorC", {"center": v(-22.68, -17.54) * mm, "radius": 0.5 * mm});
            skLineSegment(sketch, "E97.MirrorCS", {"start": v(20.5, -20.08) * mm, "end": v(17.96, -20.08) * mm, "construction": true});
            skCircle(sketch, "E98.MirrorC", {"center": v(17.96, -17.54) * mm, "radius": 0.5 * mm});
            skCircle(sketch, "E99.MirrorC", {"center": v(7.8, -4.84) * mm, "radius": 0.5 * mm});
            skCircle(sketch, "E100.MirrorC", {"center": v(-4.9, -12.46) * mm, "radius": 0.5 * mm});
            skCircle(sketch, "E101.MirrorC", {"center": v(0.18, -17.54) * mm, "radius": 0.5 * mm});
            skCircle(sketch, "E102.MirrorC", {"center": v(-9.98, -7.38) * mm, "radius": 0.5 * mm});
            skCircle(sketch, "E103.MirrorC", {"center": v(7.8, -20.08) * mm, "radius": 0.5 * mm});
            skCircle(sketch, "E104.MirrorC", {"center": v(15.42, -7.38) * mm, "radius": 0.5 * mm});
            skCircle(sketch, "E105.MirrorC", {"center": v(-7.44, -15) * mm, "radius": 0.5 * mm});
            skCircle(sketch, "E106.MirrorC", {"center": v(5.26, -4.84) * mm, "radius": 0.5 * mm});
            skCircle(sketch, "E107.MirrorC", {"center": v(5.26, -7.38) * mm, "radius": 0.5 * mm});
            skCircle(sketch, "E108.MirrorC", {"center": v(-7.44, -9.92) * mm, "radius": 0.5 * mm});
            skCircle(sketch, "E109.MirrorC", {"center": v(15.42, -12.46) * mm, "radius": 0.5 * mm});
            skCircle(sketch, "E110.MirrorC", {"center": v(-30.3, -7.38) * mm, "radius": 0.5 * mm});
            skCircle(sketch, "E111.MirrorC", {"center": v(-7.44, -12.46) * mm, "radius": 0.5 * mm});
            skCircle(sketch, "E112.MirrorC", {"center": v(-2.36, -17.54) * mm, "radius": 0.5 * mm});
            skCircle(sketch, "E113.MirrorC", {"center": v(-20.14, -17.54) * mm, "radius": 0.5 * mm});
            skCircle(sketch, "E114.MirrorC", {"center": v(15.42, -9.92) * mm, "radius": 0.5 * mm});
            skCircle(sketch, "E115.MirrorC", {"center": v(-7.44, -7.38) * mm, "radius": 0.5 * mm});
            skCircle(sketch, "E116.MirrorC", {"center": v(-37.92, -17.54) * mm, "radius": 0.5 * mm});
            skCircle(sketch, "E117.MirrorC", {"center": v(20.5, -12.46) * mm, "radius": 0.5 * mm});
            skCircle(sketch, "E118.MirrorC", {"center": v(-25.22, -7.38) * mm, "radius": 0.5 * mm});
            skCircle(sketch, "E119.MirrorC", {"center": v(-12.52, -7.38) * mm, "radius": 0.5 * mm});
            skCircle(sketch, "E120.MirrorC", {"center": v(15.42, -15) * mm, "radius": 0.5 * mm});
            skCircle(sketch, "E121.MirrorC", {"center": v(-25.22, -15) * mm, "radius": 0.5 * mm});
            skCircle(sketch, "E122.MirrorC", {"center": v(-30.3, -9.92) * mm, "radius": 0.5 * mm});
            skCircle(sketch, "E123.MirrorC", {"center": v(15.42, -17.54) * mm, "radius": 0.5 * mm});
            skCircle(sketch, "E124.MirrorC", {"center": v(-30.3, -12.46) * mm, "radius": 0.5 * mm});
            skCircle(sketch, "E125.MirrorC", {"center": v(-22.68, -4.84) * mm, "radius": 0.5 * mm});
            skCircle(sketch, "E126.MirrorC", {"center": v(-2.36, -7.38) * mm, "radius": 0.5 * mm});
            skCircle(sketch, "E127.MirrorC", {"center": v(-12.52, -12.46) * mm, "radius": 0.5 * mm});
            skCircle(sketch, "E128.MirrorC", {"center": v(-7.44, -20.08) * mm, "radius": 0.5 * mm});
            skCircle(sketch, "E129.MirrorC", {"center": v(0.18, -7.38) * mm, "radius": 0.5 * mm});
            skCircle(sketch, "E130.MirrorC", {"center": v(-12.52, -15) * mm, "radius": 0.5 * mm});
            skCircle(sketch, "E131.MirrorC", {"center": v(17.96, -7.38) * mm, "radius": 0.5 * mm});
            skCircle(sketch, "E132.MirrorC", {"center": v(-17.6, -15) * mm, "radius": 0.5 * mm});
            skCircle(sketch, "E133.MirrorC", {"center": v(5.26, -17.54) * mm, "radius": 0.5 * mm});
            skCircle(sketch, "E134.MirrorC", {"center": v(-27.76, -4.84) * mm, "radius": 0.5 * mm});
            skCircle(sketch, "E135.MirrorC", {"center": v(-35.38, -15) * mm, "radius": 0.5 * mm});
            skCircle(sketch, "E136.MirrorC", {"center": v(5.26, -15) * mm, "radius": 0.5 * mm});
            skCircle(sketch, "E137.MirrorC", {"center": v(-22.68, -7.38) * mm, "radius": 0.5 * mm});
            skCircle(sketch, "E138.MirrorC", {"center": v(-30.3, -20.08) * mm, "radius": 0.5 * mm});
            skCircle(sketch, "E139.MirrorC", {"center": v(0.18, -9.92) * mm, "radius": 0.5 * mm});
            skCircle(sketch, "E140.MirrorC", {"center": v(-4.9, -4.84) * mm, "radius": 0.5 * mm});
            skCircle(sketch, "E141.MirrorC", {"center": v(-9.98, -4.84) * mm, "radius": 0.5 * mm});
            skCircle(sketch, "E142.MirrorC", {"center": v(12.88, -12.46) * mm, "radius": 0.5 * mm});
            skCircle(sketch, "E143.MirrorC", {"center": v(-27.76, -12.46) * mm, "radius": 0.5 * mm});
            skCircle(sketch, "E144.MirrorC", {"center": v(-15.06, -4.84) * mm, "radius": 0.5 * mm});
            skCircle(sketch, "E145.MirrorC", {"center": v(-9.98, -9.92) * mm, "radius": 0.5 * mm});
            skCircle(sketch, "E146.MirrorC", {"center": v(0.18, -20.08) * mm, "radius": 0.5 * mm});
            skCircle(sketch, "E147.MirrorC", {"center": v(7.8, -7.38) * mm, "radius": 0.5 * mm});
            skCircle(sketch, "E148.MirrorC", {"center": v(5.26, -20.08) * mm, "radius": 0.5 * mm});
            skCircle(sketch, "E149.MirrorC", {"center": v(-35.38, -20.08) * mm, "radius": 0.5 * mm});
            skCircle(sketch, "E150.MirrorC", {"center": v(-15.06, -15) * mm, "radius": 0.5 * mm});
            skCircle(sketch, "E151.MirrorC", {"center": v(-20.14, -9.92) * mm, "radius": 0.5 * mm});
            skCircle(sketch, "E152.MirrorC", {"center": v(-32.84, -17.54) * mm, "radius": 0.5 * mm});
            skCircle(sketch, "E153.MirrorC", {"center": v(-22.68, -20.08) * mm, "radius": 0.5 * mm});
            skCircle(sketch, "E154.MirrorC", {"center": v(17.96, -15) * mm, "radius": 0.5 * mm});
            skCircle(sketch, "E155.MirrorC", {"center": v(-27.76, -9.92) * mm, "radius": 0.5 * mm});
            skCircle(sketch, "E156.MirrorC", {"center": v(-32.84, -12.46) * mm, "radius": 0.5 * mm});
            skCircle(sketch, "E157.MirrorC", {"center": v(-27.76, -17.54) * mm, "radius": 0.5 * mm});
            skCircle(sketch, "E158.MirrorC", {"center": v(20.5, -7.38) * mm, "radius": 0.5 * mm});
            skCircle(sketch, "E159.MirrorC", {"center": v(-9.98, -15) * mm, "radius": 0.5 * mm});
            skCircle(sketch, "E160.MirrorC", {"center": v(-20.14, -7.38) * mm, "radius": 0.5 * mm});
            skCircle(sketch, "E161.MirrorC", {"center": v(-37.92, -7.38) * mm, "radius": 0.5 * mm});
            skCircle(sketch, "E162.MirrorC", {"center": v(2.72, -9.92) * mm, "radius": 0.5 * mm});
            skCircle(sketch, "E163.MirrorC", {"center": v(20.5, -9.92) * mm, "radius": 0.5 * mm});
            skLineSegment(sketch, "E164.MirrorCS", {"start": v(20.5, -20.08) * mm, "end": v(20.5, -17.54) * mm, "construction": true});
            skCircle(sketch, "E165.MirrorC", {"center": v(-20.14, -4.84) * mm, "radius": 0.5 * mm});
            skCircle(sketch, "E166.MirrorC", {"center": v(-2.36, -4.84) * mm, "radius": 0.5 * mm});
            skCircle(sketch, "E167.MirrorC", {"center": v(-4.9, -17.54) * mm, "radius": 0.5 * mm});
            skCircle(sketch, "E168.MirrorC", {"center": v(-37.92, -12.46) * mm, "radius": 0.5 * mm});
            skCircle(sketch, "E169.MirrorC", {"center": v(12.88, -17.54) * mm, "radius": 0.5 * mm});
            skCircle(sketch, "E170.MirrorC", {"center": v(-32.84, -15) * mm, "radius": 0.5 * mm});
            skCircle(sketch, "E171.MirrorC", {"center": v(-4.9, -15) * mm, "radius": 0.5 * mm});
            skCircle(sketch, "E172.MirrorC", {"center": v(-9.98, -17.54) * mm, "radius": 0.5 * mm});
            skCircle(sketch, "E173.MirrorC", {"center": v(15.42, -4.84) * mm, "radius": 0.5 * mm});
            skCircle(sketch, "E174.MirrorC", {"center": v(-25.22, -4.84) * mm, "radius": 0.5 * mm});
            skCircle(sketch, "E175.MirrorC", {"center": v(2.72, -7.38) * mm, "radius": 0.5 * mm});
            skCircle(sketch, "E176.MirrorC", {"center": v(-12.52, -9.92) * mm, "radius": 0.5 * mm});
            skCircle(sketch, "E177.MirrorC", {"center": v(2.72, -15) * mm, "radius": 0.5 * mm});
            skCircle(sketch, "E178.MirrorC", {"center": v(7.8, -12.46) * mm, "radius": 0.5 * mm});
            skCircle(sketch, "E179.MirrorC", {"center": v(-37.92, -9.92) * mm, "radius": 0.5 * mm});
            skCircle(sketch, "E180.MirrorC", {"center": v(-15.06, -12.46) * mm, "radius": 0.5 * mm});
            skCircle(sketch, "E181.MirrorC", {"center": v(-22.68, -15) * mm, "radius": 0.5 * mm});
            skCircle(sketch, "E182.MirrorC", {"center": v(-2.36, -9.92) * mm, "radius": 0.5 * mm});
            skCircle(sketch, "E183.MirrorC", {"center": v(-15.06, -9.92) * mm, "radius": 0.5 * mm});
            skCircle(sketch, "E184.MirrorC", {"center": v(12.88, -7.38) * mm, "radius": 0.5 * mm});
            skCircle(sketch, "E185.MirrorC", {"center": v(12.88, -9.92) * mm, "radius": 0.5 * mm});
            skCircle(sketch, "E186.MirrorC", {"center": v(12.88, -20.08) * mm, "radius": 0.5 * mm});
            skCircle(sketch, "E187.MirrorC", {"center": v(2.72, -4.84) * mm, "radius": 0.5 * mm});
            skCircle(sketch, "E188.MirrorC", {"center": v(7.8, -15) * mm, "radius": 0.5 * mm});
            skCircle(sketch, "E189.MirrorC", {"center": v(7.8, -17.54) * mm, "radius": 0.5 * mm});
            skCircle(sketch, "E190.MirrorC", {"center": v(-27.76, -20.08) * mm, "radius": 0.5 * mm});
            skCircle(sketch, "E191.MirrorC", {"center": v(-4.9, -20.08) * mm, "radius": 0.5 * mm});
            skCircle(sketch, "E192.MirrorC", {"center": v(-27.76, -15) * mm, "radius": 0.5 * mm});
            skCircle(sketch, "E193.MirrorC", {"center": v(-9.98, -20.08) * mm, "radius": 0.5 * mm});
            skCircle(sketch, "E194.MirrorC", {"center": v(-15.06, -7.38) * mm, "radius": 0.5 * mm});
            skCircle(sketch, "E195.MirrorC", {"center": v(-9.98, -12.46) * mm, "radius": 0.5 * mm});
            skCircle(sketch, "E196.MirrorC", {"center": v(-17.6, -20.08) * mm, "radius": 0.5 * mm});
            skCircle(sketch, "E197.MirrorC", {"center": v(-35.38, -12.46) * mm, "radius": 0.5 * mm});
            skCircle(sketch, "E198.MirrorC", {"center": v(12.88, -15) * mm, "radius": 0.5 * mm});
            skCircle(sketch, "E199.MirrorC", {"center": v(-35.38, -17.54) * mm, "radius": 0.5 * mm});
            skCircle(sketch, "E200.MirrorC", {"center": v(7.8, -9.92) * mm, "radius": 0.5 * mm});
            skCircle(sketch, "E201.MirrorC", {"center": v(-32.84, -4.84) * mm, "radius": 0.5 * mm});
            skCircle(sketch, "E202.MirrorC", {"center": v(-32.84, -9.92) * mm, "radius": 0.5 * mm});
            skCircle(sketch, "E203.MirrorC", {"center": v(-7.44, -17.54) * mm, "radius": 0.5 * mm});
            skLineSegment(sketch, "E204.MirrorCS", {"start": v(20.5, -20.08) * mm, "end": v(20.5, -4.84) * mm, "construction": true});
            skLineSegment(sketch, "E205.MirrorCS", {"start": v(-37.92, -20.08) * mm, "end": v(-37.92, -4.84) * mm, "construction": true});
            skLineSegment(sketch, "E206.MirrorCS", {"start": v(20.5, -4.84) * mm, "end": v(-37.92, -4.84) * mm, "construction": true});
            skLineSegment(sketch, "E207.MirrorCS", {"start": v(-39, -26.58) * mm, "end": v(-39, 22.42) * mm, "construction": true});
            skLineSegment(sketch, "E208.MirrorCS", {"start": v(19, -26.58) * mm, "end": v(19, 22.42) * mm, "construction": true});
            skLineSegment(sketch, "E209.MirrorCS", {"start": v(20.5, -20.08) * mm, "end": v(-37.92, -20.08) * mm, "construction": true});
            skSolve(sketch);
        }
        {
            var Q0;
            Q0 = qSketchRegion(id + "F8", true);
            extrude(context, id + "F9", {"entities" : qUnion([Q0]), "depth" : 2 * mm});
        }
        {
            var Q0;
            Q0=makeQuery(id+"F9.opExtrude","CAP_FACE",FACE,{"disambiguationData":[OSD([sQuery(id+"F8.wireOp",EDGE,"E20.bottom"),sQuery(id+"F8.wireOp",EDGE,"E20.top"),sQuery(id+"F8.wireOp",EDGE,"E20.left"),sQuery(id+"F8.wireOp",EDGE,"E20.right"),sQuery(id+"F8.wireOp",EDGE,"E22"),sQuery(id+"F8.wireOp",EDGE,"E23"),sQuery(id+"F8.wireOp",EDGE,"E24"),sQuery(id+"F8.wireOp",EDGE,"E25"),sQuery(id+"F8.wireOp",EDGE,"E26.filletArc"),sQuery(id+"F8.wireOp",EDGE,"E27.filletArc"),sQuery(id+"F8.wireOp",EDGE,"E28.filletArc"),sQuery(id+"F8.wireOp",EDGE,"E29.filletArc"),sQuery(id+"F8.wireOp",EDGE,"E31"),sQuery(id+"F8.wireOp",EDGE,"E32.0.1.0"),sQuery(id+"F8.wireOp",EDGE,"E32.0.2.0"),sQuery(id+"F8.wireOp",EDGE,"E32.0.3.0"),sQuery(id+"F8.wireOp",EDGE,"E32.0.4.0"),sQuery(id+"F8.wireOp",EDGE,"E32.0.5.0"),sQuery(id+"F8.wireOp",EDGE,"E32.0.6.0"),sQuery(id+"F8.wireOp",EDGE,"E32.1.0.0"),sQuery(id+"F8.wireOp",EDGE,"E32.1.1.0"),sQuery(id+"F8.wireOp",EDGE,"E32.1.2.0"),sQuery(id+"F8.wireOp",EDGE,"E32.1.3.0"),sQuery(id+"F8.wireOp",EDGE,"E32.1.4.0"),sQuery(id+"F8.wireOp",EDGE,"E32.1.5.0"),sQuery(id+"F8.wireOp",EDGE,"E32.1.6.0"),sQuery(id+"F8.wireOp",EDGE,"E32.2.0.0"),sQuery(id+"F8.wireOp",EDGE,"E32.2.1.0"),sQuery(id+"F8.wireOp",EDGE,"E32.2.2.0"),sQuery(id+"F8.wireOp",EDGE,"E32.2.3.0"),sQuery(id+"F8.wireOp",EDGE,"E32.2.4.0"),sQuery(id+"F8.wireOp",EDGE,"E32.2.5.0"),sQuery(id+"F8.wireOp",EDGE,"E32.2.6.0"),sQuery(id+"F8.wireOp",EDGE,"E32.3.0.0"),sQuery(id+"F8.wireOp",EDGE,"E32.3.1.0"),sQuery(id+"F8.wireOp",EDGE,"E32.3.2.0"),sQuery(id+"F8.wireOp",EDGE,"E32.3.3.0"),sQuery(id+"F8.wireOp",EDGE,"E32.3.4.0"),sQuery(id+"F8.wireOp",EDGE,"E32.3.5.0"),sQuery(id+"F8.wireOp",EDGE,"E32.3.6.0"),sQuery(id+"F8.wireOp",EDGE,"E32.4.0.0"),sQuery(id+"F8.wireOp",EDGE,"E32.4.1.0"),sQuery(id+"F8.wireOp",EDGE,"E32.4.2.0"),sQuery(id+"F8.wireOp",EDGE,"E32.4.3.0"),sQuery(id+"F8.wireOp",EDGE,"E32.4.4.0"),sQuery(id+"F8.wireOp",EDGE,"E32.4.5.0"),sQuery(id+"F8.wireOp",EDGE,"E32.4.6.0"),sQuery(id+"F8.wireOp",EDGE,"E32.5.0.0"),sQuery(id+"F8.wireOp",EDGE,"E32.5.1.0"),sQuery(id+"F8.wireOp",EDGE,"E32.5.2.0"),sQuery(id+"F8.wireOp",EDGE,"E32.5.3.0"),sQuery(id+"F8.wireOp",EDGE,"E32.5.4.0"),sQuery(id+"F8.wireOp",EDGE,"E32.5.5.0"),sQuery(id+"F8.wireOp",EDGE,"E32.5.6.0"),sQuery(id+"F8.wireOp",EDGE,"E32.6.0.0"),sQuery(id+"F8.wireOp",EDGE,"E32.6.1.0"),sQuery(id+"F8.wireOp",EDGE,"E32.6.2.0"),sQuery(id+"F8.wireOp",EDGE,"E32.6.3.0"),sQuery(id+"F8.wireOp",EDGE,"E32.6.4.0"),sQuery(id+"F8.wireOp",EDGE,"E32.6.5.0"),sQuery(id+"F8.wireOp",EDGE,"E32.6.6.0"),sQuery(id+"F8.wireOp",EDGE,"E32.7.0.0"),sQuery(id+"F8.wireOp",EDGE,"E32.7.1.0"),sQuery(id+"F8.wireOp",EDGE,"E32.7.2.0"),sQuery(id+"F8.wireOp",EDGE,"E32.7.3.0"),sQuery(id+"F8.wireOp",EDGE,"E32.7.4.0"),sQuery(id+"F8.wireOp",EDGE,"E32.7.5.0"),sQuery(id+"F8.wireOp",EDGE,"E32.7.6.0"),sQuery(id+"F8.wireOp",EDGE,"E32.8.0.0"),sQuery(id+"F8.wireOp",EDGE,"E32.8.1.0"),sQuery(id+"F8.wireOp",EDGE,"E32.8.2.0"),sQuery(id+"F8.wireOp",EDGE,"E32.8.3.0"),sQuery(id+"F8.wireOp",EDGE,"E32.8.4.0"),sQuery(id+"F8.wireOp",EDGE,"E32.8.5.0"),sQuery(id+"F8.wireOp",EDGE,"E32.8.6.0"),sQuery(id+"F8.wireOp",EDGE,"E32.9.0.0"),sQuery(id+"F8.wireOp",EDGE,"E32.9.1.0"),sQuery(id+"F8.wireOp",EDGE,"E32.9.2.0"),sQuery(id+"F8.wireOp",EDGE,"E32.9.3.0"),sQuery(id+"F8.wireOp",EDGE,"E32.9.4.0"),sQuery(id+"F8.wireOp",EDGE,"E32.9.5.0"),sQuery(id+"F8.wireOp",EDGE,"E32.9.6.0"),sQuery(id+"F8.wireOp",EDGE,"E32.10.0.0"),sQuery(id+"F8.wireOp",EDGE,"E32.10.1.0"),sQuery(id+"F8.wireOp",EDGE,"E32.10.2.0"),sQuery(id+"F8.wireOp",EDGE,"E32.10.3.0"),sQuery(id+"F8.wireOp",EDGE,"E32.10.4.0"),sQuery(id+"F8.wireOp",EDGE,"E32.10.5.0"),sQuery(id+"F8.wireOp",EDGE,"E32.10.6.0"),sQuery(id+"F8.wireOp",EDGE,"E32.11.0.0"),sQuery(id+"F8.wireOp",EDGE,"E32.11.1.0"),sQuery(id+"F8.wireOp",EDGE,"E32.11.2.0"),sQuery(id+"F8.wireOp",EDGE,"E32.11.3.0"),sQuery(id+"F8.wireOp",EDGE,"E32.11.4.0"),sQuery(id+"F8.wireOp",EDGE,"E32.11.5.0"),sQuery(id+"F8.wireOp",EDGE,"E32.11.6.0"),sQuery(id+"F8.wireOp",EDGE,"E32.12.0.0"),sQuery(id+"F8.wireOp",EDGE,"E32.12.1.0"),sQuery(id+"F8.wireOp",EDGE,"E32.12.2.0"),sQuery(id+"F8.wireOp",EDGE,"E32.12.3.0"),sQuery(id+"F8.wireOp",EDGE,"E32.12.4.0"),sQuery(id+"F8.wireOp",EDGE,"E32.12.5.0"),sQuery(id+"F8.wireOp",EDGE,"E32.12.6.0"),sQuery(id+"F8.wireOp",EDGE,"E32.13.0.0"),sQuery(id+"F8.wireOp",EDGE,"E32.13.1.0"),sQuery(id+"F8.wireOp",EDGE,"E32.13.2.0"),sQuery(id+"F8.wireOp",EDGE,"E32.13.3.0"),sQuery(id+"F8.wireOp",EDGE,"E32.13.4.0"),sQuery(id+"F8.wireOp",EDGE,"E32.13.5.0"),sQuery(id+"F8.wireOp",EDGE,"E32.13.6.0"),sQuery(id+"F8.wireOp",EDGE,"E32.14.0.0"),sQuery(id+"F8.wireOp",EDGE,"E32.14.1.0"),sQuery(id+"F8.wireOp",EDGE,"E32.14.2.0"),sQuery(id+"F8.wireOp",EDGE,"E32.14.3.0"),sQuery(id+"F8.wireOp",EDGE,"E32.14.4.0"),sQuery(id+"F8.wireOp",EDGE,"E32.14.5.0"),sQuery(id+"F8.wireOp",EDGE,"E32.14.6.0"),sQuery(id+"F8.wireOp",EDGE,"E32.15.0.0"),sQuery(id+"F8.wireOp",EDGE,"E32.15.1.0"),sQuery(id+"F8.wireOp",EDGE,"E32.15.2.0"),sQuery(id+"F8.wireOp",EDGE,"E32.15.3.0"),sQuery(id+"F8.wireOp",EDGE,"E32.15.4.0"),sQuery(id+"F8.wireOp",EDGE,"E32.15.5.0"),sQuery(id+"F8.wireOp",EDGE,"E32.15.6.0"),sQuery(id+"F8.wireOp",EDGE,"E32.16.0.0"),sQuery(id+"F8.wireOp",EDGE,"E32.16.1.0"),sQuery(id+"F8.wireOp",EDGE,"E32.16.2.0"),sQuery(id+"F8.wireOp",EDGE,"E32.16.3.0"),sQuery(id+"F8.wireOp",EDGE,"E32.16.4.0"),sQuery(id+"F8.wireOp",EDGE,"E32.16.5.0"),sQuery(id+"F8.wireOp",EDGE,"E32.16.6.0"),sQuery(id+"F8.wireOp",EDGE,"E32.17.0.0"),sQuery(id+"F8.wireOp",EDGE,"E32.17.1.0"),sQuery(id+"F8.wireOp",EDGE,"E32.17.2.0"),sQuery(id+"F8.wireOp",EDGE,"E32.17.3.0"),sQuery(id+"F8.wireOp",EDGE,"E32.17.4.0"),sQuery(id+"F8.wireOp",EDGE,"E32.17.5.0"),sQuery(id+"F8.wireOp",EDGE,"E32.17.6.0"),sQuery(id+"F8.wireOp",EDGE,"E32.18.0.0"),sQuery(id+"F8.wireOp",EDGE,"E32.18.1.0"),sQuery(id+"F8.wireOp",EDGE,"E32.18.2.0"),sQuery(id+"F8.wireOp",EDGE,"E32.18.3.0"),sQuery(id+"F8.wireOp",EDGE,"E32.18.4.0"),sQuery(id+"F8.wireOp",EDGE,"E32.18.5.0"),sQuery(id+"F8.wireOp",EDGE,"E32.18.6.0"),sQuery(id+"F8.wireOp",EDGE,"E32.19.0.0"),sQuery(id+"F8.wireOp",EDGE,"E32.19.1.0"),sQuery(id+"F8.wireOp",EDGE,"E32.19.2.0"),sQuery(id+"F8.wireOp",EDGE,"E32.19.3.0"),sQuery(id+"F8.wireOp",EDGE,"E32.19.4.0"),sQuery(id+"F8.wireOp",EDGE,"E32.19.5.0"),sQuery(id+"F8.wireOp",EDGE,"E32.19.6.0"),sQuery(id+"F8.wireOp",EDGE,"E32.20.0.0"),sQuery(id+"F8.wireOp",EDGE,"E32.20.1.0"),sQuery(id+"F8.wireOp",EDGE,"E32.20.2.0"),sQuery(id+"F8.wireOp",EDGE,"E32.20.3.0"),sQuery(id+"F8.wireOp",EDGE,"E32.20.4.0"),sQuery(id+"F8.wireOp",EDGE,"E32.20.5.0"),sQuery(id+"F8.wireOp",EDGE,"E32.20.6.0"),sQuery(id+"F8.wireOp",EDGE,"E32.21.0.0"),sQuery(id+"F8.wireOp",EDGE,"E32.21.1.0"),sQuery(id+"F8.wireOp",EDGE,"E32.21.2.0"),sQuery(id+"F8.wireOp",EDGE,"E32.21.3.0"),sQuery(id+"F8.wireOp",EDGE,"E32.21.4.0"),sQuery(id+"F8.wireOp",EDGE,"E32.21.5.0"),sQuery(id+"F8.wireOp",EDGE,"E32.21.6.0"),sQuery(id+"F8.wireOp",EDGE,"E32.22.0.0"),sQuery(id+"F8.wireOp",EDGE,"E32.22.1.0"),sQuery(id+"F8.wireOp",EDGE,"E32.22.2.0"),sQuery(id+"F8.wireOp",EDGE,"E32.22.3.0"),sQuery(id+"F8.wireOp",EDGE,"E32.22.4.0"),sQuery(id+"F8.wireOp",EDGE,"E32.22.5.0"),sQuery(id+"F8.wireOp",EDGE,"E32.22.6.0"),sQuery(id+"F8.wireOp",EDGE,"E32.23.0.0"),sQuery(id+"F8.wireOp",EDGE,"E32.23.1.0"),sQuery(id+"F8.wireOp",EDGE,"E32.23.2.0"),sQuery(id+"F8.wireOp",EDGE,"E32.23.3.0"),sQuery(id+"F8.wireOp",EDGE,"E32.23.4.0"),sQuery(id+"F8.wireOp",EDGE,"E32.23.5.0"),sQuery(id+"F8.wireOp",EDGE,"E32.23.6.0"),sQuery(id+"F8.wireOp",EDGE,"E34.MirrorC"),sQuery(id+"F8.wireOp",EDGE,"E35.MirrorC"),sQuery(id+"F8.wireOp",EDGE,"E36.MirrorC"),sQuery(id+"F8.wireOp",EDGE,"E37.MirrorC"),sQuery(id+"F8.wireOp",EDGE,"E38.MirrorC"),sQuery(id+"F8.wireOp",EDGE,"E39.MirrorC"),sQuery(id+"F8.wireOp",EDGE,"E40.MirrorC"),sQuery(id+"F8.wireOp",EDGE,"E41.MirrorC"),sQuery(id+"F8.wireOp",EDGE,"E42.MirrorC"),sQuery(id+"F8.wireOp",EDGE,"E43.MirrorC"),sQuery(id+"F8.wireOp",EDGE,"E44.MirrorC"),sQuery(id+"F8.wireOp",EDGE,"E45.MirrorC"),sQuery(id+"F8.wireOp",EDGE,"E46.MirrorC"),sQuery(id+"F8.wireOp",EDGE,"E47.MirrorC"),sQuery(id+"F8.wireOp",EDGE,"E48.MirrorC"),sQuery(id+"F8.wireOp",EDGE,"E49.MirrorC"),sQuery(id+"F8.wireOp",EDGE,"E50.MirrorC"),sQuery(id+"F8.wireOp",EDGE,"E51.MirrorC"),sQuery(id+"F8.wireOp",EDGE,"E52.MirrorC"),sQuery(id+"F8.wireOp",EDGE,"E53.MirrorC"),sQuery(id+"F8.wireOp",EDGE,"E54.MirrorC"),sQuery(id+"F8.wireOp",EDGE,"E55.MirrorC"),sQuery(id+"F8.wireOp",EDGE,"E56.MirrorC"),sQuery(id+"F8.wireOp",EDGE,"E57.MirrorC"),sQuery(id+"F8.wireOp",EDGE,"E58.MirrorC"),sQuery(id+"F8.wireOp",EDGE,"E59.MirrorC"),sQuery(id+"F8.wireOp",EDGE,"E60.MirrorC"),sQuery(id+"F8.wireOp",EDGE,"E61.MirrorC"),sQuery(id+"F8.wireOp",EDGE,"E62.MirrorC"),sQuery(id+"F8.wireOp",EDGE,"E63.MirrorC"),sQuery(id+"F8.wireOp",EDGE,"E64.MirrorC"),sQuery(id+"F8.wireOp",EDGE,"E65.MirrorC"),sQuery(id+"F8.wireOp",EDGE,"E66.MirrorC"),sQuery(id+"F8.wireOp",EDGE,"E67.MirrorC"),sQuery(id+"F8.wireOp",EDGE,"E68.MirrorC"),sQuery(id+"F8.wireOp",EDGE,"E69.MirrorC"),sQuery(id+"F8.wireOp",EDGE,"E70.MirrorC"),sQuery(id+"F8.wireOp",EDGE,"E71.MirrorC"),sQuery(id+"F8.wireOp",EDGE,"E72.MirrorC"),sQuery(id+"F8.wireOp",EDGE,"E73.MirrorC"),sQuery(id+"F8.wireOp",EDGE,"E74.MirrorC"),sQuery(id+"F8.wireOp",EDGE,"E75.MirrorC"),sQuery(id+"F8.wireOp",EDGE,"E76.MirrorC"),sQuery(id+"F8.wireOp",EDGE,"E77.MirrorC"),sQuery(id+"F8.wireOp",EDGE,"E78.MirrorC"),sQuery(id+"F8.wireOp",EDGE,"E79.MirrorC"),sQuery(id+"F8.wireOp",EDGE,"E80.MirrorC"),sQuery(id+"F8.wireOp",EDGE,"E81.MirrorC"),sQuery(id+"F8.wireOp",EDGE,"E82.MirrorC"),sQuery(id+"F8.wireOp",EDGE,"E83.MirrorC"),sQuery(id+"F8.wireOp",EDGE,"E84.MirrorC"),sQuery(id+"F8.wireOp",EDGE,"E85.MirrorC"),sQuery(id+"F8.wireOp",EDGE,"E86.MirrorC"),sQuery(id+"F8.wireOp",EDGE,"E87.MirrorC"),sQuery(id+"F8.wireOp",EDGE,"E88.MirrorC"),sQuery(id+"F8.wireOp",EDGE,"E89.MirrorC"),sQuery(id+"F8.wireOp",EDGE,"E90.MirrorC"),sQuery(id+"F8.wireOp",EDGE,"E91.MirrorC"),sQuery(id+"F8.wireOp",EDGE,"E92.MirrorC"),sQuery(id+"F8.wireOp",EDGE,"E93.MirrorC"),sQuery(id+"F8.wireOp",EDGE,"E94.MirrorC"),sQuery(id+"F8.wireOp",EDGE,"E95.MirrorC"),sQuery(id+"F8.wireOp",EDGE,"E96.MirrorC"),sQuery(id+"F8.wireOp",EDGE,"E98.MirrorC"),sQuery(id+"F8.wireOp",EDGE,"E99.MirrorC"),sQuery(id+"F8.wireOp",EDGE,"E100.MirrorC"),sQuery(id+"F8.wireOp",EDGE,"E101.MirrorC"),sQuery(id+"F8.wireOp",EDGE,"E102.MirrorC"),sQuery(id+"F8.wireOp",EDGE,"E103.MirrorC"),sQuery(id+"F8.wireOp",EDGE,"E104.MirrorC"),sQuery(id+"F8.wireOp",EDGE,"E105.MirrorC"),sQuery(id+"F8.wireOp",EDGE,"E106.MirrorC"),sQuery(id+"F8.wireOp",EDGE,"E107.MirrorC"),sQuery(id+"F8.wireOp",EDGE,"E108.MirrorC"),sQuery(id+"F8.wireOp",EDGE,"E109.MirrorC"),sQuery(id+"F8.wireOp",EDGE,"E110.MirrorC"),sQuery(id+"F8.wireOp",EDGE,"E111.MirrorC"),sQuery(id+"F8.wireOp",EDGE,"E112.MirrorC"),sQuery(id+"F8.wireOp",EDGE,"E113.MirrorC"),sQuery(id+"F8.wireOp",EDGE,"E114.MirrorC"),sQuery(id+"F8.wireOp",EDGE,"E115.MirrorC"),sQuery(id+"F8.wireOp",EDGE,"E116.MirrorC"),sQuery(id+"F8.wireOp",EDGE,"E117.MirrorC"),sQuery(id+"F8.wireOp",EDGE,"E118.MirrorC"),sQuery(id+"F8.wireOp",EDGE,"E119.MirrorC"),sQuery(id+"F8.wireOp",EDGE,"E120.MirrorC"),sQuery(id+"F8.wireOp",EDGE,"E121.MirrorC"),sQuery(id+"F8.wireOp",EDGE,"E122.MirrorC"),sQuery(id+"F8.wireOp",EDGE,"E123.MirrorC"),sQuery(id+"F8.wireOp",EDGE,"E124.MirrorC"),sQuery(id+"F8.wireOp",EDGE,"E125.MirrorC"),sQuery(id+"F8.wireOp",EDGE,"E126.MirrorC"),sQuery(id+"F8.wireOp",EDGE,"E127.MirrorC"),sQuery(id+"F8.wireOp",EDGE,"E128.MirrorC"),sQuery(id+"F8.wireOp",EDGE,"E129.MirrorC"),sQuery(id+"F8.wireOp",EDGE,"E130.MirrorC"),sQuery(id+"F8.wireOp",EDGE,"E131.MirrorC"),sQuery(id+"F8.wireOp",EDGE,"E132.MirrorC"),sQuery(id+"F8.wireOp",EDGE,"E133.MirrorC"),sQuery(id+"F8.wireOp",EDGE,"E134.MirrorC"),sQuery(id+"F8.wireOp",EDGE,"E135.MirrorC"),sQuery(id+"F8.wireOp",EDGE,"E136.MirrorC"),sQuery(id+"F8.wireOp",EDGE,"E137.MirrorC"),sQuery(id+"F8.wireOp",EDGE,"E138.MirrorC"),sQuery(id+"F8.wireOp",EDGE,"E139.MirrorC"),sQuery(id+"F8.wireOp",EDGE,"E140.MirrorC"),sQuery(id+"F8.wireOp",EDGE,"E141.MirrorC"),sQuery(id+"F8.wireOp",EDGE,"E142.MirrorC"),sQuery(id+"F8.wireOp",EDGE,"E143.MirrorC"),sQuery(id+"F8.wireOp",EDGE,"E144.MirrorC"),sQuery(id+"F8.wireOp",EDGE,"E145.MirrorC"),sQuery(id+"F8.wireOp",EDGE,"E146.MirrorC"),sQuery(id+"F8.wireOp",EDGE,"E147.MirrorC"),sQuery(id+"F8.wireOp",EDGE,"E148.MirrorC"),sQuery(id+"F8.wireOp",EDGE,"E149.MirrorC"),sQuery(id+"F8.wireOp",EDGE,"E150.MirrorC"),sQuery(id+"F8.wireOp",EDGE,"E151.MirrorC"),sQuery(id+"F8.wireOp",EDGE,"E152.MirrorC"),sQuery(id+"F8.wireOp",EDGE,"E153.MirrorC"),sQuery(id+"F8.wireOp",EDGE,"E154.MirrorC"),sQuery(id+"F8.wireOp",EDGE,"E155.MirrorC"),sQuery(id+"F8.wireOp",EDGE,"E156.MirrorC"),sQuery(id+"F8.wireOp",EDGE,"E157.MirrorC"),sQuery(id+"F8.wireOp",EDGE,"E158.MirrorC"),sQuery(id+"F8.wireOp",EDGE,"E159.MirrorC"),sQuery(id+"F8.wireOp",EDGE,"E160.MirrorC"),sQuery(id+"F8.wireOp",EDGE,"E161.MirrorC"),sQuery(id+"F8.wireOp",EDGE,"E162.MirrorC"),sQuery(id+"F8.wireOp",EDGE,"E163.MirrorC"),sQuery(id+"F8.wireOp",EDGE,"E165.MirrorC"),sQuery(id+"F8.wireOp",EDGE,"E166.MirrorC"),sQuery(id+"F8.wireOp",EDGE,"E167.MirrorC"),sQuery(id+"F8.wireOp",EDGE,"E168.MirrorC"),sQuery(id+"F8.wireOp",EDGE,"E169.MirrorC"),sQuery(id+"F8.wireOp",EDGE,"E170.MirrorC"),sQuery(id+"F8.wireOp",EDGE,"E171.MirrorC"),sQuery(id+"F8.wireOp",EDGE,"E172.MirrorC"),sQuery(id+"F8.wireOp",EDGE,"E173.MirrorC"),sQuery(id+"F8.wireOp",EDGE,"E174.MirrorC"),sQuery(id+"F8.wireOp",EDGE,"E175.MirrorC"),sQuery(id+"F8.wireOp",EDGE,"E176.MirrorC"),sQuery(id+"F8.wireOp",EDGE,"E177.MirrorC"),sQuery(id+"F8.wireOp",EDGE,"E178.MirrorC"),sQuery(id+"F8.wireOp",EDGE,"E179.MirrorC"),sQuery(id+"F8.wireOp",EDGE,"E180.MirrorC"),sQuery(id+"F8.wireOp",EDGE,"E181.MirrorC"),sQuery(id+"F8.wireOp",EDGE,"E182.MirrorC"),sQuery(id+"F8.wireOp",EDGE,"E183.MirrorC"),sQuery(id+"F8.wireOp",EDGE,"E184.MirrorC"),sQuery(id+"F8.wireOp",EDGE,"E185.MirrorC"),sQuery(id+"F8.wireOp",EDGE,"E186.MirrorC"),sQuery(id+"F8.wireOp",EDGE,"E187.MirrorC"),sQuery(id+"F8.wireOp",EDGE,"E188.MirrorC"),sQuery(id+"F8.wireOp",EDGE,"E189.MirrorC"),sQuery(id+"F8.wireOp",EDGE,"E190.MirrorC"),sQuery(id+"F8.wireOp",EDGE,"E191.MirrorC"),sQuery(id+"F8.wireOp",EDGE,"E192.MirrorC"),sQuery(id+"F8.wireOp",EDGE,"E193.MirrorC"),sQuery(id+"F8.wireOp",EDGE,"E194.MirrorC"),sQuery(id+"F8.wireOp",EDGE,"E195.MirrorC"),sQuery(id+"F8.wireOp",EDGE,"E196.MirrorC"),sQuery(id+"F8.wireOp",EDGE,"E197.MirrorC"),sQuery(id+"F8.wireOp",EDGE,"E198.MirrorC"),sQuery(id+"F8.wireOp",EDGE,"E199.MirrorC"),sQuery(id+"F8.wireOp",EDGE,"E200.MirrorC"),sQuery(id+"F8.wireOp",EDGE,"E201.MirrorC"),sQuery(id+"F8.wireOp",EDGE,"E202.MirrorC"),sQuery(id+"F8.wireOp",EDGE,"E203.MirrorC")])],"isStart":false});
            var sketch = newSketch(context, id + "F10", { "sketchPlane" : qUnion([Q0])});
            skLineSegment(sketch, "E210.bottom", {"start": v(-37.92, 2.76) * mm, "end": v(-20.14, 2.76) * mm});
            skLineSegment(sketch, "E210.top", {"start": v(-37.92, -4.84) * mm, "end": v(-20.14, -4.84) * mm});
            skLineSegment(sketch, "E210.left", {"start": v(-37.92, 2.76) * mm, "end": v(-37.92, -4.84) * mm});
            skLineSegment(sketch, "E210.right", {"start": v(-20.14, 2.76) * mm, "end": v(-20.14, -4.84) * mm});
            skLineSegment(sketch, "E211.bottom", {"start": v(-15.06, 2.76) * mm, "end": v(2.72, 2.76) * mm});
            skLineSegment(sketch, "E211.top", {"start": v(-15.06, -4.84) * mm, "end": v(2.72, -4.84) * mm});
            skLineSegment(sketch, "E211.left", {"start": v(-15.06, 2.76) * mm, "end": v(-15.06, -4.84) * mm});
            skLineSegment(sketch, "E211.right", {"start": v(2.72, 2.76) * mm, "end": v(2.72, -4.84) * mm});
            skSolve(sketch);
        }
        {
            var Q0;
            Q0 = qSketchRegion(id + "F10", true);
            extrude(context, id + "F11", {"entities" : qUnion([Q0]), "depth" : 3 * mm, "offsetDistance" : 25 * mm});
        }
    });
